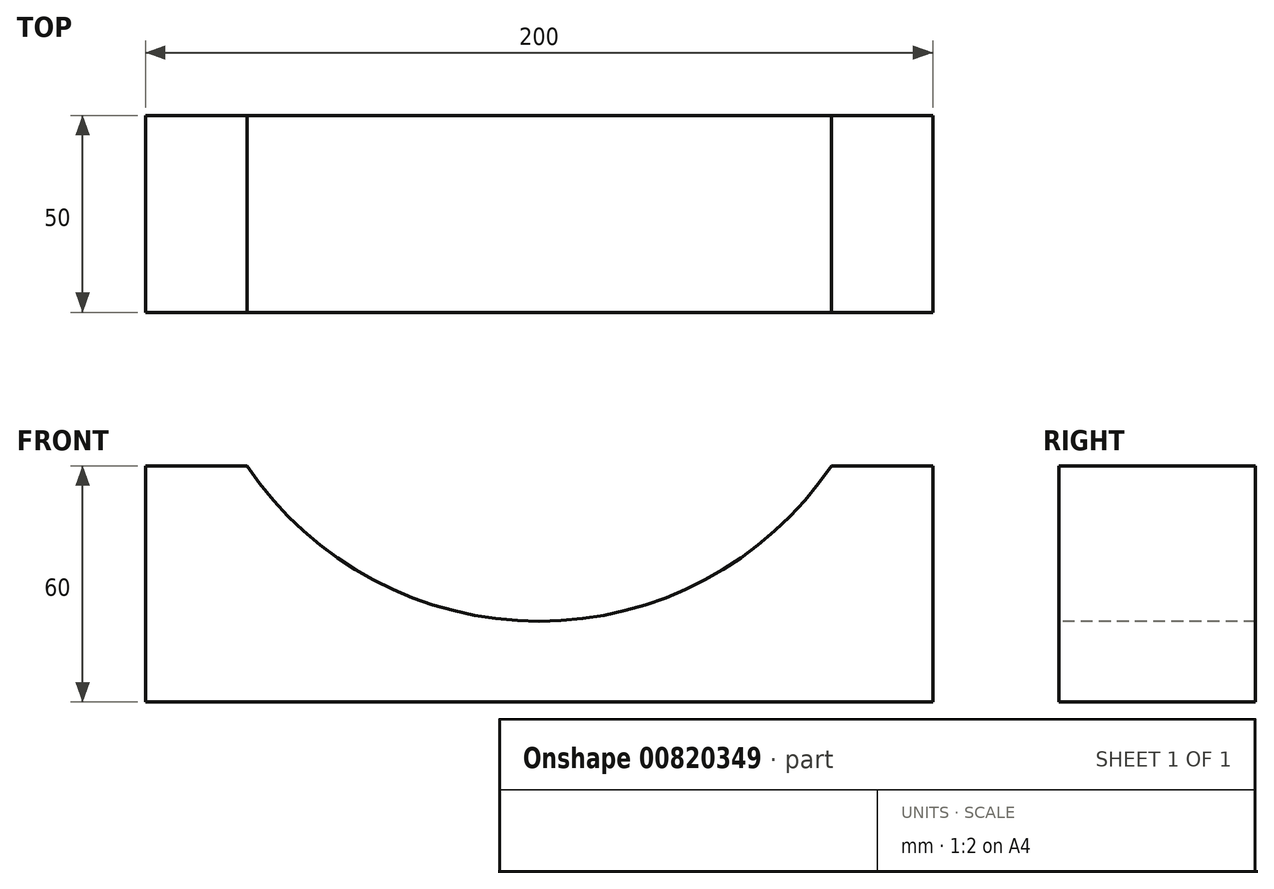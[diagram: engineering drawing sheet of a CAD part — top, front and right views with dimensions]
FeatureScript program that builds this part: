
annotation { "Feature Type Name" : "Feature", "Feature Type Description" : "" }
export const myFeature = defineFeature(function(context is Context, id is Id, definition is map)
    precondition{}
    {
        {
            var Q0;
            Q0=qCreatedBy(makeId("Front.planeOp"),FACE);
            var sketch = newSketch(context, id + "F0", { "sketchPlane" : qUnion([Q0])});
            skArc(sketch, "E0", {"start": v(-74.23, -50) * mm, "mid": v(0, -89.5) * mm, "end": v(74.23, -50) * mm});
            skLineSegment(sketch, "E1.bottom", {"start": v(-100, -50) * mm, "end": v(-74.23, -50) * mm});
            skLineSegment(sketch, "E1.top", {"start": v(-100, -110) * mm, "end": v(100, -110) * mm});
            skLineSegment(sketch, "E1.left", {"start": v(-100, -50) * mm, "end": v(-100, -110) * mm});
            skLineSegment(sketch, "E1.right", {"start": v(100, -50) * mm, "end": v(100, -110) * mm});
            skLineSegment(sketch, "E2.trimOffspring", {"start": v(74.23, -50) * mm, "end": v(100, -50) * mm});
            skSolve(sketch);
        }
        {
            var Q0;
            Q0 = qSketchRegion(id + "F0", true);
            extrude(context, id + "F1", {"entities" : qUnion([Q0]), "oppositeDirection" : true, "depth" : 50 * mm, "offsetDistance" : 25 * mm});
        }
    });
